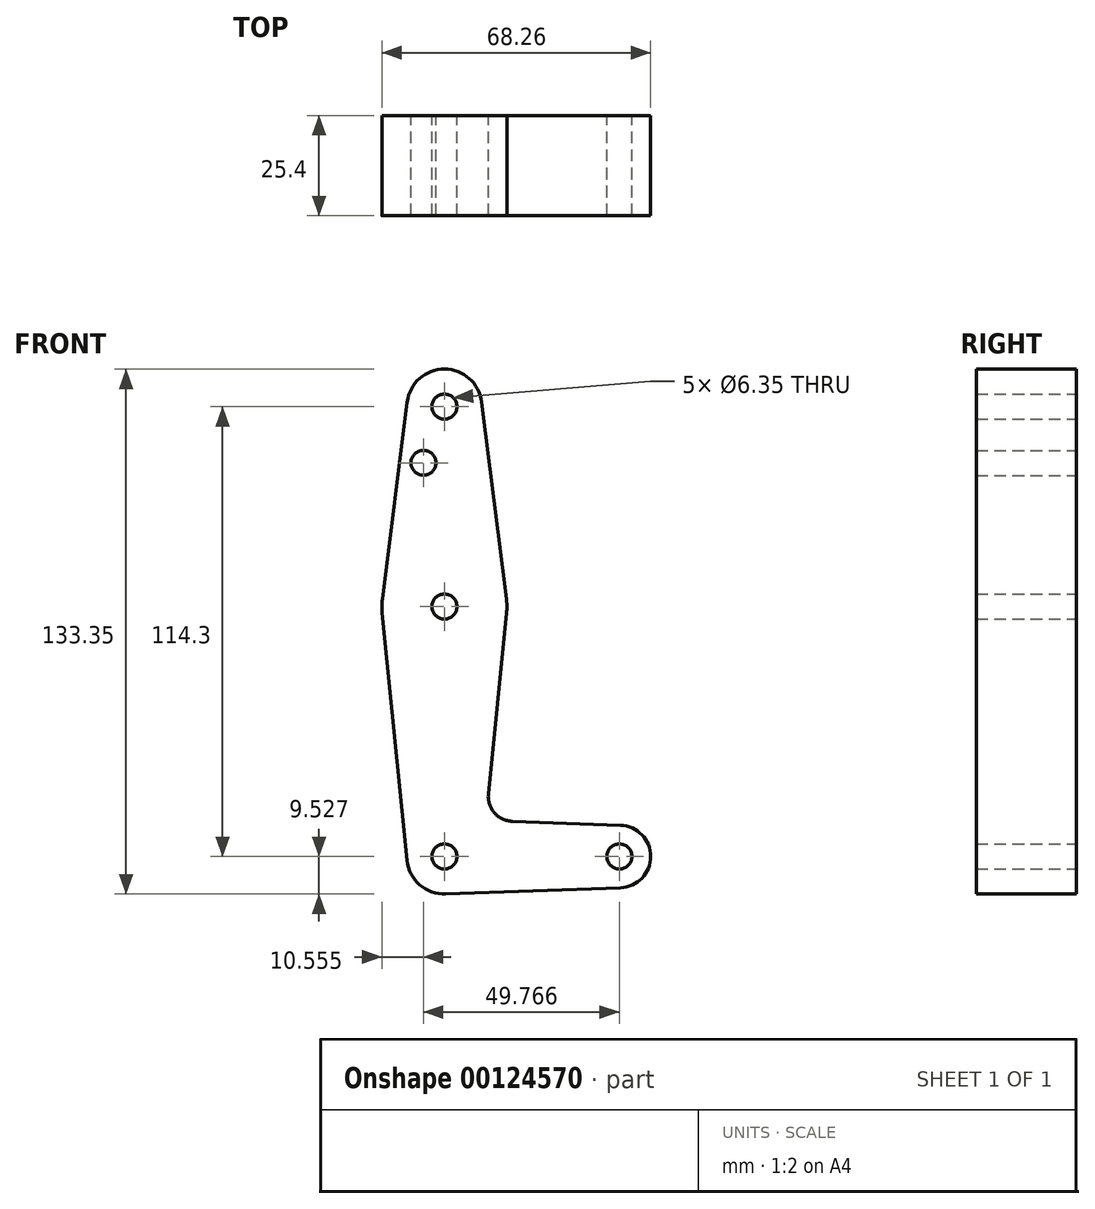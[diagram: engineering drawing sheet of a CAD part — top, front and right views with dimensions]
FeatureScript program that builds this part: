
annotation { "Feature Type Name" : "Feature", "Feature Type Description" : "" }
export const myFeature = defineFeature(function(context is Context, id is Id, definition is map)
    precondition{}
    {
        {
            var Q0;
            Q0=qCreatedBy(makeId("Front.planeOp"),FACE);
            var sketch = newSketch(context, id + "F0", { "sketchPlane" : qUnion([Q0])});
            skCircle(sketch, "E0", {"center": v(-37.25, 84.32) * mm, "radius": 9.53 * mm});
            skCircle(sketch, "E1", {"center": v(-37.25, 33.52) * mm, "radius": 15.88 * mm});
            skCircle(sketch, "E2", {"center": v(-37.25, -29.98) * mm, "radius": 9.53 * mm});
            skCircle(sketch, "E3", {"center": v(7.2, -29.98) * mm, "radius": 7.94 * mm});
            skLineSegment(sketch, "E4", {"start": v(-37.25, 84.32) * mm, "end": v(-37.25, 33.52) * mm, "construction": true});
            skLineSegment(sketch, "E5", {"start": v(-37.25, 33.52) * mm, "end": v(-37.25, -29.98) * mm, "construction": true});
            skLineSegment(sketch, "E6", {"start": v(-37.25, -29.98) * mm, "end": v(7.2, -29.98) * mm, "construction": true});
            skLineSegment(sketch, "E7", {"start": v(-36.9, -39.5) * mm, "end": v(7.48, -37.92) * mm});
            skLineSegment(sketch, "E8", {"start": v(-19.99, -21.07) * mm, "end": v(7.48, -22.05) * mm});
            skLineSegment(sketch, "E9", {"start": v(-46.7, 85.5) * mm, "end": v(-53, 35.5) * mm});
            skLineSegment(sketch, "E10", {"start": v(-27.8, 85.5) * mm, "end": v(-21.5, 35.5) * mm});
            skLineSegment(sketch, "E11", {"start": v(-53.04, 31.93) * mm, "end": v(-46.73, -30.94) * mm});
            skLineSegment(sketch, "E12", {"start": v(-21.45, 31.93) * mm, "end": v(-26.08, -14.09) * mm});
            skCircle(sketch, "E13", {"center": v(-37.25, 84.32) * mm, "radius": 3.18 * mm});
            skCircle(sketch, "E14", {"center": v(-42.57, 70.04) * mm, "radius": 3.18 * mm});
            skCircle(sketch, "E15", {"center": v(-37.25, 33.52) * mm, "radius": 3.18 * mm});
            skCircle(sketch, "E16", {"center": v(-37.25, -29.98) * mm, "radius": 3.18 * mm});
            skCircle(sketch, "E17", {"center": v(7.2, -29.98) * mm, "radius": 3.18 * mm});
            skArc(sketch, "E18.filletArc", {"start": v(-26.08, -14.09) * mm, "mid": v(-24.54, -18.9) * mm, "end": v(-19.99, -21.07) * mm});
            skSolve(sketch);
        }
        {
            var Q0;
            Q0=makeQuery(id+"F0.imprint","IMPRINT",FACE,{"disambiguationData":[TD([[makeQuery(id+"F0.imprint","IMPRINT",EDGE,{"derivedFrom":sQuery(id+"F0.wireOp",EDGE,"E13")}),-1.0]])]});
            var Q1;
            {var subQ1=sQuery(id+"F0.wireOp",EDGE,"E9");Q1=makeQuery(id+"F0.imprint","IMPRINT",FACE,{"disambiguationData":[TD([[makeQuery(id+"F0.imprint","IMPRINT",EDGE,{"derivedFrom":subQ1}),1.0]])]});}
            var Q2;
            Q2=makeQuery(id+"F0.imprint","IMPRINT",FACE,{"disambiguationData":[TD([[makeQuery(id+"F0.imprint","IMPRINT",EDGE,{"derivedFrom":sQuery(id+"F0.wireOp",EDGE,"E15")}),-1.0]])]});
            var Q3;
            {var subQ0=sQuery(id+"F0.wireOp",EDGE,"E7");Q3=makeQuery(id+"F0.imprint","IMPRINT",FACE,{"disambiguationData":[TD([[makeQuery(id+"F0.imprint","IMPRINT",EDGE,{"derivedFrom":subQ0}),1.0]])]});}
            var Q4;
            Q4=makeQuery(id+"F0.imprint","IMPRINT",FACE,{"disambiguationData":[TD([[makeQuery(id+"F0.imprint","IMPRINT",EDGE,{"derivedFrom":sQuery(id+"F0.wireOp",EDGE,"E16")}),-1.0]])]});
            var Q5;
            Q5=makeQuery(id+"F0.imprint","IMPRINT",FACE,{"disambiguationData":[TD([[makeQuery(id+"F0.imprint","IMPRINT",EDGE,{"derivedFrom":sQuery(id+"F0.wireOp",EDGE,"E17")}),-1.0]])]});
            extrude(context, id + "F1", {"entities" : qUnion([Q0, Q1, Q2, Q3, Q4, Q5]), "depth" : 25.4 * mm});
        }
    });
